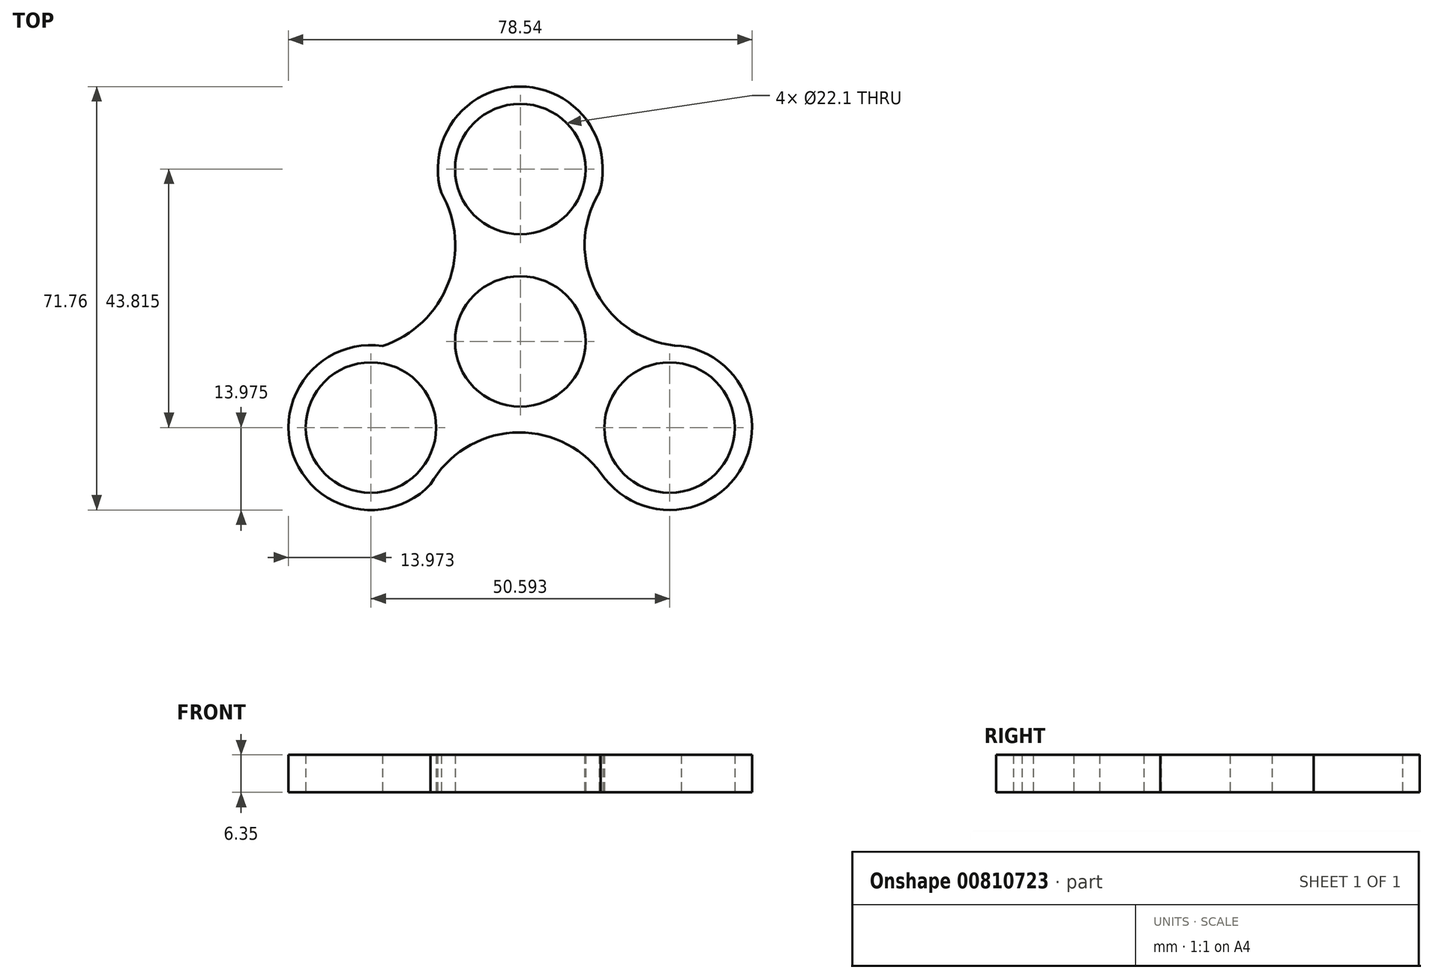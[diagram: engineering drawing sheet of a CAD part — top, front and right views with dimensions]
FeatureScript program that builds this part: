
annotation { "Feature Type Name" : "Feature", "Feature Type Description" : "" }
export const myFeature = defineFeature(function(context is Context, id is Id, definition is map)
    precondition{}
    {
        {
            var Q0;
            Q0=qCreatedBy(makeId("Top.planeOp"),FACE);
            var sketch = newSketch(context, id + "F0", { "sketchPlane" : qUnion([Q0])});
            skCircle(sketch, "E0", {"center": v(0, 0) * mm, "radius": 44.45 * mm});
            skCircle(sketch, "E1", {"center": v(0, 0) * mm, "radius": 11.05 * mm});
            skLineSegment(sketch, "E2", {"start": v(0, 0) * mm, "end": v(0, 29.21) * mm});
            skCircle(sketch, "E3", {"center": v(0, 29.21) * mm, "radius": 11.05 * mm});
            skCircle(sketch, "E4.1.0", {"center": v(-25.3, -14.6) * mm, "radius": 11.05 * mm});
            skCircle(sketch, "E4.2.0", {"center": v(25.3, -14.6) * mm, "radius": 11.05 * mm});
            skCircle(sketch, "E5", {"center": v(0, 29.21) * mm, "radius": 13.97 * mm});
            skCircle(sketch, "E6", {"center": v(25.3, -14.6) * mm, "radius": 13.97 * mm});
            skCircle(sketch, "E7", {"center": v(-25.3, -14.6) * mm, "radius": 13.97 * mm});
            skCircle(sketch, "E8", {"center": v(0, 0) * mm, "radius": 13.97 * mm});
            skArc(sketch, "E9", {"start": v(13.38, 25.19) * mm, "mid": v(12.93, 8.24) * mm, "end": v(27.28, -0.78) * mm});
            skArc(sketch, "E10", {"start": v(13.65, -22.31) * mm, "mid": v(-1.29, -15.46) * mm, "end": v(-15.18, -24.24) * mm});
            skArc(sketch, "E11", {"start": v(-23.31, -0.78) * mm, "mid": v(-12.2, 9.85) * mm, "end": v(-13.38, 25.19) * mm});
            skSolve(sketch);
        }
        {
            var Q0;
            Q0=makeQuery(id+"F0.imprint","IMPRINT",FACE,{"disambiguationData":[TD([[makeQuery(id+"F0.imprint","IMPRINT",EDGE,{"derivedFrom":sQuery(id+"F0.wireOp",EDGE,"E8")}),-1.0]])]});
            extrude(context, id + "F1", {"entities" : qUnion([Q0]), "depth" : 6.35 * mm, "offsetDistance" : 25.4 * mm});
        }
        {
            var Q0;
            Q0=makeQuery(id+"F0.imprint","IMPRINT",FACE,{"disambiguationData":[TD([[makeQuery(id+"F0.imprint","IMPRINT",EDGE,{"derivedFrom":sQuery(id+"F0.wireOp",EDGE,"E4.1.0")}),-1.0]])]});
            extrude(context, id + "F2", {"entities" : qUnion([Q0]), "operationType" : NewBodyOperationType.ADD, "depth" : 6.35 * mm, "offsetDistance" : 25.4 * mm});
        }
        {
            var Q0;
            Q0=makeQuery(id+"F0.imprint","IMPRINT",FACE,{"disambiguationData":[TD([[makeQuery(id+"F0.imprint","IMPRINT",EDGE,{"derivedFrom":sQuery(id+"F0.wireOp",EDGE,"E4.2.0")}),-1.0]])]});
            extrude(context, id + "F3", {"entities" : qUnion([Q0]), "operationType" : NewBodyOperationType.ADD, "depth" : 6.35 * mm, "offsetDistance" : 25.4 * mm});
        }
        {
            var Q0;
            Q0=makeQuery(id+"F0.imprint","IMPRINT",FACE,{"disambiguationData":[TD([[makeQuery(id+"F0.imprint","IMPRINT",EDGE,{"derivedFrom":sQuery(id+"F0.wireOp",EDGE,"E3")}),-1.0]])]});
            extrude(context, id + "F4", {"entities" : qUnion([Q0]), "operationType" : NewBodyOperationType.ADD, "depth" : 6.35 * mm, "offsetDistance" : 25.4 * mm});
        }
        {
            var Q0;
            Q0=makeQuery(id+"F0.imprint","IMPRINT",FACE,{"disambiguationData":[TD([[makeQuery(id+"F0.imprint","IMPRINT",EDGE,{"derivedFrom":sQuery(id+"F0.wireOp",EDGE,"E1")}),-1.0]])]});
            extrude(context, id + "F5", {"entities" : qUnion([Q0]), "operationType" : NewBodyOperationType.ADD, "depth" : 6.35 * mm, "offsetDistance" : 25.4 * mm});
        }
    });
